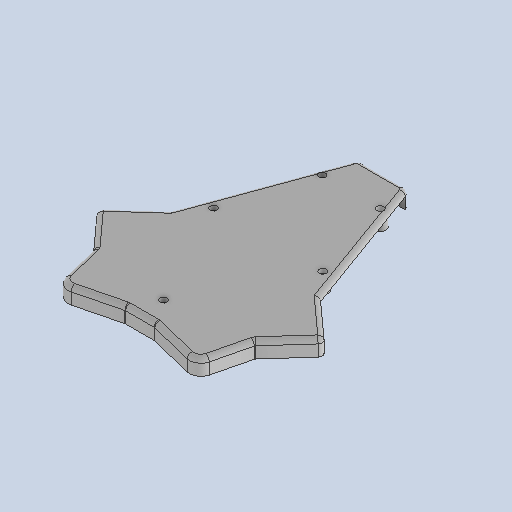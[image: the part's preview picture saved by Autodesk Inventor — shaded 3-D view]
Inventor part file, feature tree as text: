
AUTODESK INVENTOR PART (.ipt)
format: ipt  version: 2024 (Build 280153000, 153)  size: 306,688 bytes
history: native  units: mm
features: reference x24, extrude x6, sketch x6, other x6, plane x2, fillet x1, projected_geometry x1
ambient origin geometry x8: Origin, YZ Plane, XZ Plane, XY Plane, X Axis, Y Axis, Z Axis, Center Point
bodies: Volumenkörper1 (feature_tree)
feature tree (46):
  extrude  "Extrusion1"  Depth=5.0mm TaperAngle=0.0deg
  extrude  "Extrusion2"  Depth=2.5mm
  fillet  "Rundung1"  Radius=12.0mm
  extrude  "Extrusion3"  Depth=10.0mm TaperAngle=0.0deg
  sketch  "Skizze4"  dims[d11=3.1mm d12=3.1mm]
  plane  "Arbeitsebene1"
  extrude  "Extrusion4"  Depth=3.1mm
  extrude  "Extrusion5"  Depth=3.1mm
  sketch  "Skizze6"  dims[d15=3.1mm d16=2.2mm d17=0.0mm d18=5.0mm d19=5.0mm d20=5.0mm d21=5.0mm d22=5.0mm d23=2.0mm d24=0.0mm]
  plane  "Arbeitsebene2"
  extrude  "Extrusion6"  Depth=5.0mm TaperAngle=0.0deg
  sketch  "Skizze1"  dims[d0=5.0mm d1=0.0mm d2=2.0mm d3=0.0mm]
  reference  "Referenz1"
  reference  "Referenz2"
  reference  "Referenz3"
  reference  "Referenz4"
  reference  "Referenz5"
  reference  "Referenz6"
  reference  "Referenz7"
  reference  "Referenz8"
  reference  "Referenz9"
  reference  "Referenz10"
  sketch  "Skizze2"  dims[d4=2.0mm d5=2.5mm d6=12.0mm]
  projected_geometry  "Projizierte Kontur1"
  sketch  "Skizze3"  dims[d7=2.0mm d8=0.0mm d9=10.0mm d10=0.0mm]
  reference  "Referenz11"
  reference  "Referenz12"
  reference  "Referenz13"
  reference  "Referenz14"
  reference  "Referenz15"
  sketch  "Skizze5"  dims[d13=3.1mm d14=3.1mm]
  reference  "Referenz16"
  reference  "Referenz17"
  reference  "Referenz18"
  reference  "Referenz19"
  reference  "Referenz20"
  reference  "Referenz21"
  reference  "Referenz22"
  reference  "Referenz23"
  reference  "Referenz24"
  other  "<userpath>\OneDrive\Keyboards\Blavinge\case\case.iam"
  other  "case.iam"
  other  "middle_top:1"
  other  "blavinge:1"
  other  "left_bottom_MIR:1"
  other  "left_bottom:1"
